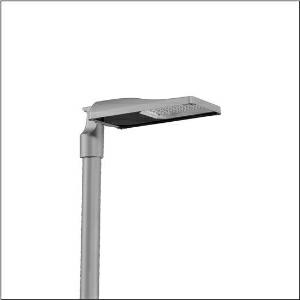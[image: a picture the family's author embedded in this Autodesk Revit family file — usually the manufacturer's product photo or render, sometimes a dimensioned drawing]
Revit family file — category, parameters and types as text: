
# Revit family: streetlight_sl_31_mini___st1_0a_5xh6d31a08ja_4a04
name_source: partatom
category: Lighting Fixtures
units: mm (PartAtom-declared; Revit-internal decimal feet)

## family parameters
Cut with Voids When Loaded = No
Host = Face
Light Source = No
Part Type = Normal
Room Calculation Point = No
Round Connector Dimension = Use Diameter
Shared = No

## types (1)
- --- (1 x LED, 12140 lm, 81.1 W, 3000K)
    Apparent Load = 81 VA
    CIE Flux Codes = 40 73 97 100 100
    Color Rendering = 70
    Color Temperature = 3000K
    Default Elevation = 1800 mm
    Description = Streetlight SL 31 mini Easy, Desk-Remote mast luminaire for post-top, side-entry; light control with lens of PMMA; light distribution: ST1.0a, direct asymmetric distribution, for standard-compliant lighting for roads and squares; LED: luminous flux: 12.140lm, light colour: 730, colour temperature: 3000K; luminous efficacy: 149,7lm/W; control: pre-setting: linear dimming characteristic, flexible luminous flux parameterisation, time-dependent luminous flux control, constant luminous flux control, intelligent temperature release in ECG and LED module, overheat protection; luminaire housing, of diecast aluminium, SITECO metallic grey (DB 702S), corrosivity category C5 high according to DIN EN ISO 12944; cover of toughened safety glass, transparent, opened without tools; mast flange of diecast aluminium, SITECO metallic grey (DB 702S), spigot size: 76/60mm, mast flange included unmounted; with cable H07RN-F 2x 1.5mm², cable length: 10,5m, connection cable pre-assembled; mains connection: 220..240V, AC, 50/60Hz; power consumption (at start of service life): 81,1W / (at end of service life): 88,3W / (with reduced operation 50%): 36,4W; protection rating (complete): IP66; insulation class (complete): insulation class II (safety insulation); impact resistance: IK10; certification: CE, ENEC, ENEC+, VDE, UKCA; permissible operating ambient temperature for outdoor applications: -40..+50°C; packaging unit: 1 piece

Light Distribution: ST1.0a
    Height = 76 mm
    Lamp = 1 x LED
    Lamp Light Flux = 12140 lm
    Lamp Power = 81.1 W
    Lamp count = 1
    Length = 547 mm
    Luminous efficacy = 150 lm/W
    Manufacturer = Siteco
    ModVariant = No
    Model = 5XH6D31A08JA
    Number of Poles = 1
    OnlyDefault = Yes
    Power Factor = 1
    Product Name = Streetlight SL 31 mini | ST1.0a
    Product group = mast luminaire | pylon top
    ProductGroupID = 6100
    Protection Class = Protection class II
    Protection Degree = IP 66
    RLX_Detail_Level = 1
    RLX_Emergency_Light_Flux = 0 lm
    RLX_Emergency_Type = 0
    RLX_Emergency_Type_DB = No
    RlxData = <blob elided: 39733 chars, md5=a9107357>
    Socket = socket
    Standby Power = 0 W
    System Light Flux = 12140 lm
    System Power = 81 W
    Type Comments = factory setting: luminous flux: 100 % | dim-lin: 254 | 860 mA
    Type Image = l_1300326.jpg
    URL = http://relux.com
    VarID = @adj_057395
    Voltage = 0 V
    Weight = 0.00 kg
    Width = 265 mm

## geometry (parser evidence)
native form markers: Blend x4, Sweep x8
no freeform markers — native parametric forms only
